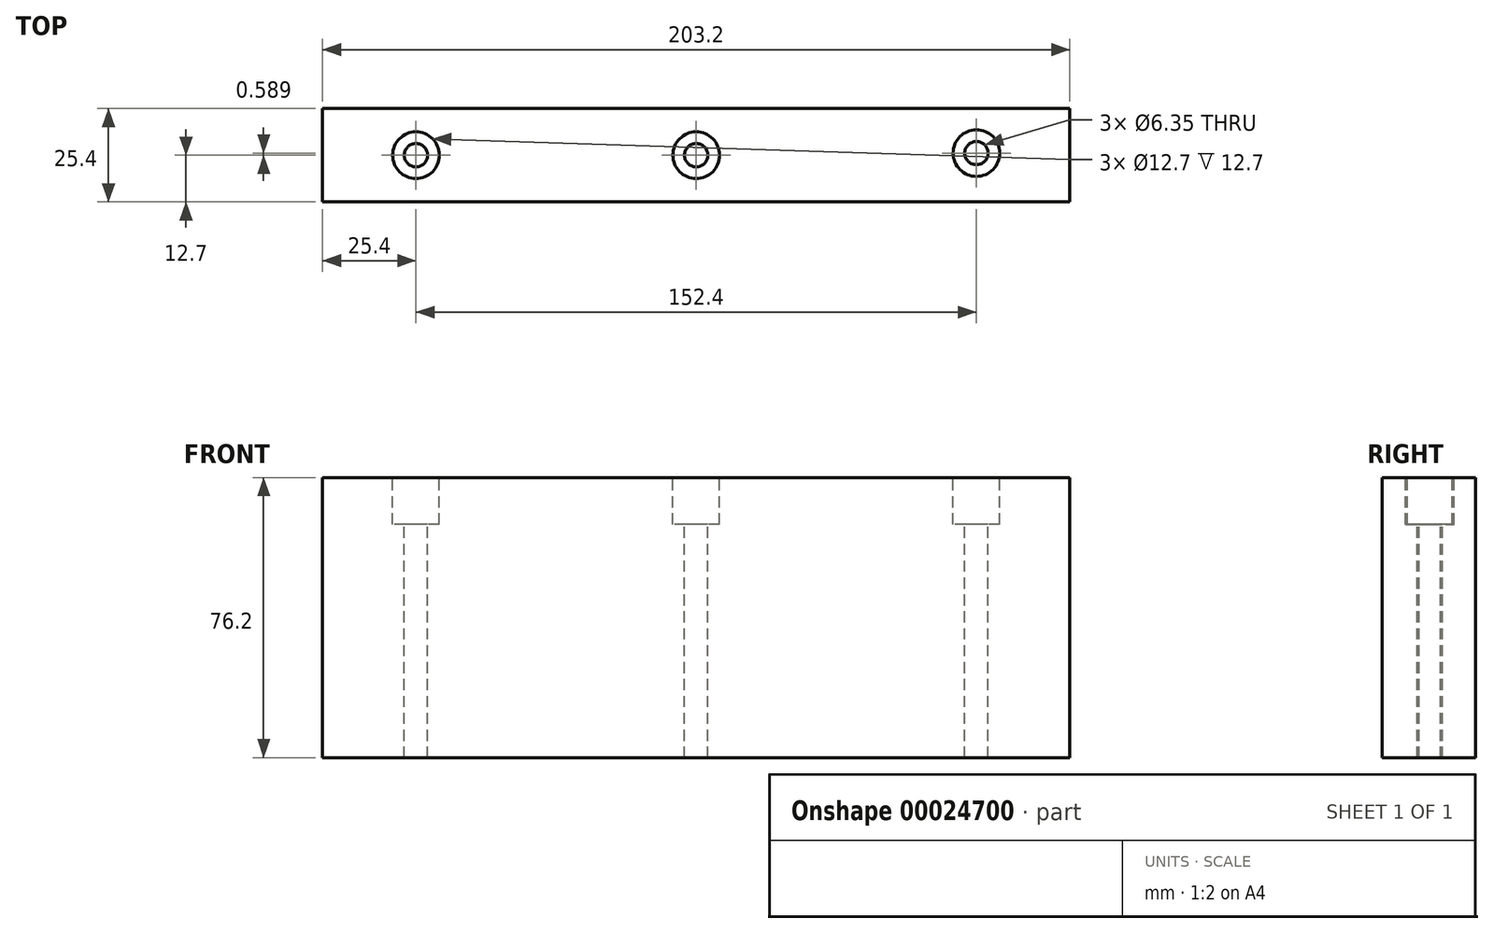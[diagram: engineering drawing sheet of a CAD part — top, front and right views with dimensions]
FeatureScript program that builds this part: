
annotation { "Feature Type Name" : "Feature", "Feature Type Description" : "" }
export const myFeature = defineFeature(function(context is Context, id is Id, definition is map)
    precondition{}
    {
        {
            var Q0;
            Q0=qCreatedBy(makeId("Front.planeOp"),FACE);
            var sketch = newSketch(context, id + "F0", { "sketchPlane" : qUnion([Q0])});
            skLineSegment(sketch, "E0.bottom", {"start": v(0, 0) * mm, "end": v(203.2, 0) * mm});
            skLineSegment(sketch, "E0.top", {"start": v(0, 76.2) * mm, "end": v(203.2, 76.2) * mm});
            skLineSegment(sketch, "E0.left", {"start": v(0, 0) * mm, "end": v(0, 76.2) * mm});
            skLineSegment(sketch, "E0.right", {"start": v(203.2, 0) * mm, "end": v(203.2, 76.2) * mm});
            skSolve(sketch);
        }
        {
            var Q0;
            Q0 = qSketchRegion(id + "F0", true);
            extrude(context, id + "F1", {"entities" : qUnion([Q0]), "oppositeDirection" : true, "depth" : 25.4 * mm});
        }
        {
            var Q0;
            Q0=makeQuery(id+"F1.opExtrude","SWEPT_FACE",FACE,{"disambiguationData":[OSD([sQuery(id+"F0.wireOp",EDGE,"E0.top")])]});
            var sketch = newSketch(context, id + "F2", { "sketchPlane" : qUnion([Q0])});
            skCircle(sketch, "E1", {"center": v(25.4, 12.7) * mm, "radius": 3.18 * mm});
            skCircle(sketch, "E2.1.0.0", {"center": v(101.6, 12.7) * mm, "radius": 3.18 * mm});
            skCircle(sketch, "E2.2.0.0", {"center": v(177.8, 13.29) * mm, "radius": 3.18 * mm});
            skLineSegment(sketch, "E2.direction1", {"start": v(25.4, 12.7) * mm, "end": v(101.6, 12.7) * mm, "construction": true});
            skSolve(sketch);
        }
        {
            var Q0;
            Q0=sQuery(id+"F2.wireOp",VERTEX,"E2.1.0.0.center");
            var Q1;
            Q1=sQuery(id+"F2.wireOp",VERTEX,"E2.2.0.0.center");
            var Q2;
            Q2=sQuery(id+"F2.wireOp",VERTEX,"E1.center");
            var Q3;
            Q3=makeQuery(id+"F1.opExtrude","SWEPT_BODY",BODY,{"disambiguationData":[OSD([sQuery(id+"F0.wireOp",EDGE,"E0.bottom"),sQuery(id+"F0.wireOp",EDGE,"E0.top"),sQuery(id+"F0.wireOp",EDGE,"E0.left"),sQuery(id+"F0.wireOp",EDGE,"E0.right")])]});
            hole(context, id + "F3", {"style" : HoleStyle.C_BORE, "holeDiameter" : 6.35 * mm, "cBoreDiameter" : 12.7 * mm, "cBoreDepth" : 12.7 * mm, "endStyle" : HoleEndStyle.THROUGH, "locations" : qUnion([Q0, Q1, Q2]), "scope" : qUnion([Q3])});
        }
    });
